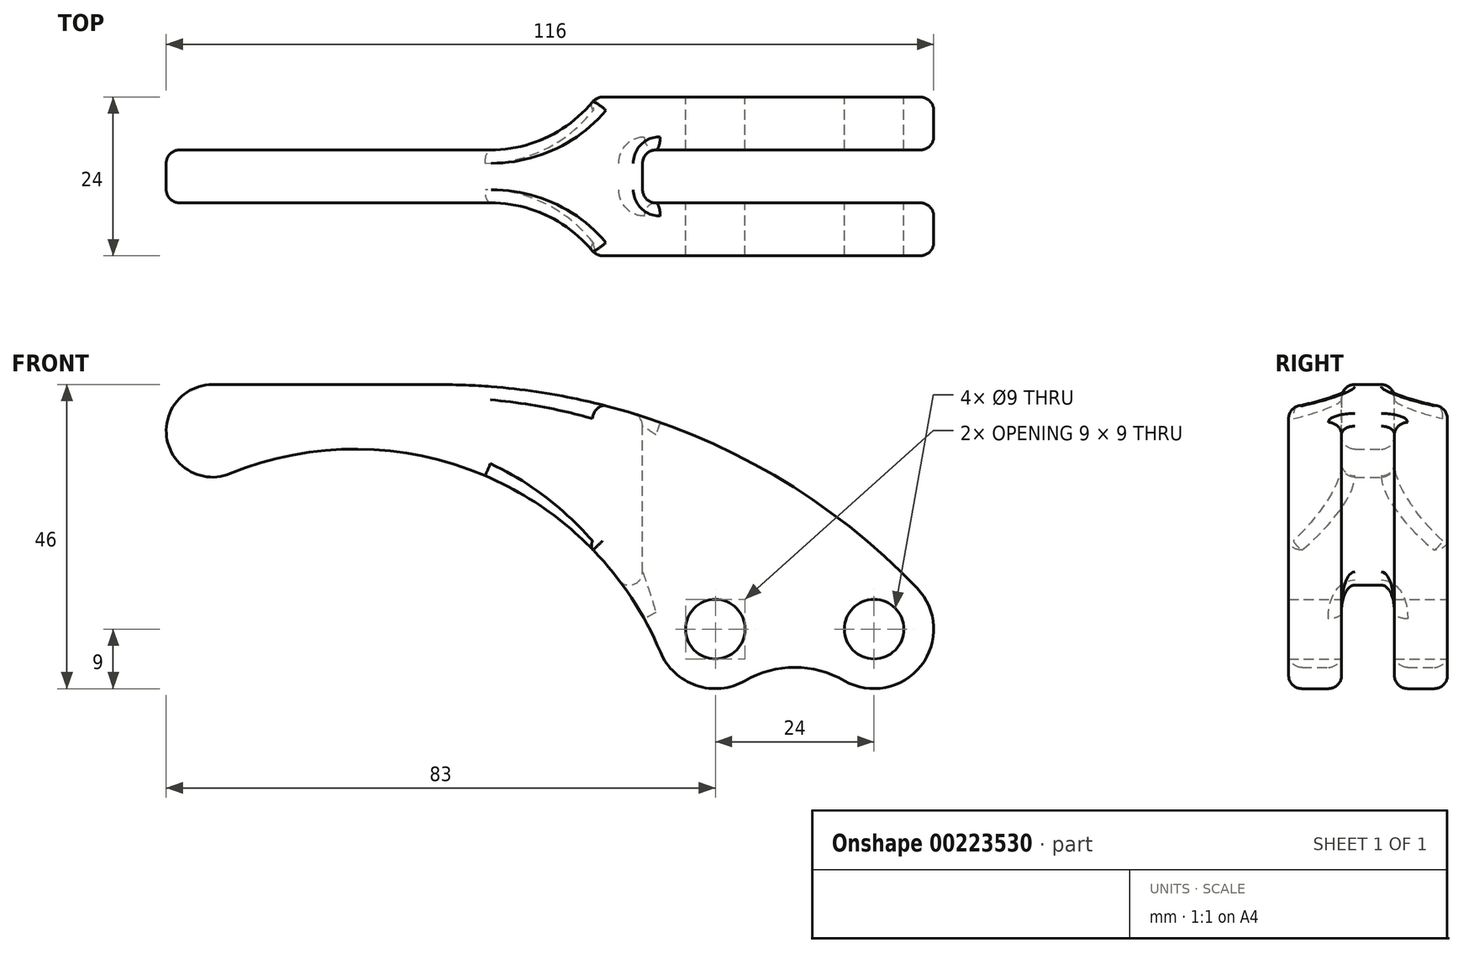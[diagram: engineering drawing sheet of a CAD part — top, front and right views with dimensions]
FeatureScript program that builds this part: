
annotation { "Feature Type Name" : "Feature", "Feature Type Description" : "" }
export const myFeature = defineFeature(function(context is Context, id is Id, definition is map)
    precondition{}
    {
        {
            var Q0;
            Q0=qCreatedBy(makeId("Front.planeOp"),FACE);
            var sketch = newSketch(context, id + "F0", { "sketchPlane" : qUnion([Q0])});
            skCircle(sketch, "E0", {"center": v(0, 0) * mm, "radius": 7 * mm});
            skCircle(sketch, "E1", {"center": v(76, -30) * mm, "radius": 4.5 * mm});
            skCircle(sketch, "E2", {"center": v(76, -30) * mm, "radius": 9 * mm});
            skCircle(sketch, "E3", {"center": v(100, -30) * mm, "radius": 4.5 * mm});
            skCircle(sketch, "E4", {"center": v(100, -30) * mm, "radius": 9 * mm});
            skLineSegment(sketch, "E5", {"start": v(0, 7) * mm, "end": v(34.33, 7) * mm});
            skArc(sketch, "E6", {"start": v(106.5, -23.77) * mm, "mid": v(73.56, -1.01) * mm, "end": v(34.33, 7) * mm});
            skArc(sketch, "E7", {"start": v(95.5, -37.8) * mm, "mid": v(88, -35.78) * mm, "end": v(80.5, -37.8) * mm});
            skArc(sketch, "E8", {"start": v(67.7, -33.47) * mm, "mid": v(40.73, -6.58) * mm, "end": v(2.65, -6.48) * mm});
            skSolve(sketch);
        }
        {
            var Q0;
            Q0=qSketchRegion(id+"F0",true);
            extrude(context, id + "F1", {"entities" : qUnion([Q0]), "depth" : 24 * mm, "symmetric" : true});
        }
        {
            var Q0;
            Q0=qCreatedBy(makeId("Top.planeOp"),FACE);
            var sketch = newSketch(context, id + "F2", { "sketchPlane" : qUnion([Q0])});
            skLineSegment(sketch, "E9", {"start": v(-7, -4) * mm, "end": v(42, -4) * mm});
            skArc(sketch, "E10", {"start": v(58, -12) * mm, "mid": v(50.94, -6.11) * mm, "end": v(42, -4) * mm});
            skLineSegment(sketch, "E11", {"start": v(-7, -12) * mm, "end": v(-7, -4) * mm});
            skLineSegment(sketch, "E12.0", {"start": v(58, -12) * mm, "end": v(-7, -12) * mm});
            skPoint(sketch, "E13.orphan", {"position": v(106.5, -12) * mm});
            skSolve(sketch);
        }
        {
            var Q0;
            Q0=qSketchRegion(id+"F2",true);
            extrude(context, id + "F3", {"entities" : qUnion([Q0]), "oppositeDirection" : true, "depth" : 50 * mm, "symmetric" : true});
        }
        {
            var Q0;
            Q0=makeQuery(id+"F3.opExtrude","SWEPT_BODY",BODY,{"disambiguationData":[OSD([sQuery(id+"F2.wireOp",EDGE,"E9"),sQuery(id+"F2.wireOp",EDGE,"E10"),sQuery(id+"F2.wireOp",EDGE,"E11"),sQuery(id+"F2.wireOp",EDGE,"E12.0")])]});
            var Q1;
            Q1=qCreatedBy(makeId("Front.planeOp"),FACE);
            mirror(context, id + "F4", {"entities" : qUnion([Q0]), "mirrorPlane" : qUnion([Q1])});
        }
        {
            var Q0;
            Q0=makeQuery(id+"F4.opPattern","COPY",BODY,{"derivedFrom":makeQuery(id+"F3.opExtrude","SWEPT_BODY",BODY,{"disambiguationData":[OSD([sQuery(id+"F2.wireOp",EDGE,"E9"),sQuery(id+"F2.wireOp",EDGE,"E10"),sQuery(id+"F2.wireOp",EDGE,"E11"),sQuery(id+"F2.wireOp",EDGE,"E12.0")])]}),"instanceName":"1"});
            var Q1;
            Q1=makeQuery(id+"F3.opExtrude","SWEPT_BODY",BODY,{"disambiguationData":[OSD([sQuery(id+"F2.wireOp",EDGE,"E9"),sQuery(id+"F2.wireOp",EDGE,"E10"),sQuery(id+"F2.wireOp",EDGE,"E11"),sQuery(id+"F2.wireOp",EDGE,"E12.0")])]});
            var Q2;
            Q2=makeQuery(id+"F1.opExtrude","SWEPT_BODY",BODY,{"disambiguationData":[OSD([sQuery(id+"F0.wireOp",EDGE,"E0"),sQuery(id+"F0.wireOp",EDGE,"E1"),sQuery(id+"F0.wireOp",EDGE,"E2"),sQuery(id+"F0.wireOp",EDGE,"E3"),sQuery(id+"F0.wireOp",EDGE,"E4"),sQuery(id+"F0.wireOp",EDGE,"E5"),sQuery(id+"F0.wireOp",EDGE,"E6"),sQuery(id+"F0.wireOp",EDGE,"E7"),sQuery(id+"F0.wireOp",EDGE,"E8")])]});
            booleanBodies(context, id + "F5", {"operationType" : BooleanOperationType.SUBTRACTION, "tools" : qUnion([Q0, Q1]), "targets" : qUnion([Q2])});
        }
        {
            var Q0;
            Q0=makeQuery(id+"F1.opExtrude","SWEPT_FACE",FACE,{"disambiguationData":[OSD([sQuery(id+"F0.wireOp",EDGE,"E5")])]});
            var sketch = newSketch(context, id + "F6", { "sketchPlane" : qUnion([Q0])});
            skLineSegment(sketch, "E14.bottom", {"start": v(109, -4) * mm, "end": v(65, -4) * mm});
            skLineSegment(sketch, "E14.top", {"start": v(109, 4) * mm, "end": v(65, 4) * mm});
            skLineSegment(sketch, "E14.left", {"start": v(109, -4) * mm, "end": v(109, 4) * mm});
            skLineSegment(sketch, "E14.right", {"start": v(65, -4) * mm, "end": v(65, 4) * mm});
            skPoint(sketch, "E14.middle", {"position": v(87, 0) * mm});
            skLineSegment(sketch, "E15", {"start": v(109, 12) * mm, "end": v(109, -12) * mm, "construction": true});
            skSolve(sketch);
        }
        {
            var Q0;
            Q0=qSketchRegion(id+"F6",true);
            extrude(context, id + "F7", {"entities" : qUnion([Q0]), "operationType" : NewBodyOperationType.REMOVE, "endBound" : BoundingType.THROUGH_ALL, "oppositeDirection" : true, "depth" : 25 * mm});
        }
        {
            var Q0;
            Q0=makeQuery(id+"F1.opExtrude","SWEPT_FACE",FACE,{"disambiguationData":[OSD([sQuery(id+"F0.wireOp",EDGE,"E0")])]});
            var Q1;
            Q1=makeQuery(id+"F5.opBoolean","COPY",FACE,{"derivedFrom":makeQuery(id+"F3.opExtrude","SWEPT_FACE",FACE,{"disambiguationData":[OSD([sQuery(id+"F2.wireOp",EDGE,"E10")])]})});
            var Q2;
            {var subQ2=sQuery(id+"F0.wireOp",EDGE,"E4");Q2=makeQuery(id+"F7.boolean.opBoolean","SPLIT",FACE,{"disambiguationData":[TD([makeQuery(id+"F7.opExtrude","SWEPT_FACE",FACE,{"disambiguationData":[OSD([sQuery(id+"F6.wireOp",EDGE,"E14.bottom")])]})])],"derivedFrom":makeQuery(id+"F1.opExtrude","SWEPT_FACE",FACE,{"disambiguationData":[OSD([subQ2])]})});}
            var Q3;
            {var subQ2=sQuery(id+"F0.wireOp",EDGE,"E4");Q3=makeQuery(id+"F7.boolean.opBoolean","SPLIT",FACE,{"disambiguationData":[TD([makeQuery(id+"F7.opExtrude","SWEPT_FACE",FACE,{"disambiguationData":[OSD([sQuery(id+"F6.wireOp",EDGE,"E14.top")])]})])],"derivedFrom":makeQuery(id+"F1.opExtrude","SWEPT_FACE",FACE,{"disambiguationData":[OSD([subQ2])]})});}
            var Q4;
            Q4=makeQuery(id+"F7.boolean.opBoolean","COPY",FACE,{"derivedFrom":makeQuery(id+"F7.opExtrude","SWEPT_FACE",FACE,{"disambiguationData":[OSD([sQuery(id+"F6.wireOp",EDGE,"E14.right")])]})});
            var Q5;
            Q5=makeQuery(id+"F5.opBoolean","COPY",FACE,{"derivedFrom":makeQuery(id+"F4.opPattern","COPY",FACE,{"derivedFrom":makeQuery(id+"F3.opExtrude","SWEPT_FACE",FACE,{"disambiguationData":[OSD([sQuery(id+"F2.wireOp",EDGE,"E10")])]}),"instanceName":"1"})});
            fillet(context, id + "F8", {"entities" : qUnion([Q0, Q1, Q2, Q3, Q4, Q5]), "radius" : 2 * mm, "tangentPropagation" : true, "allowEdgeOverflow" : false});
        }
    });
